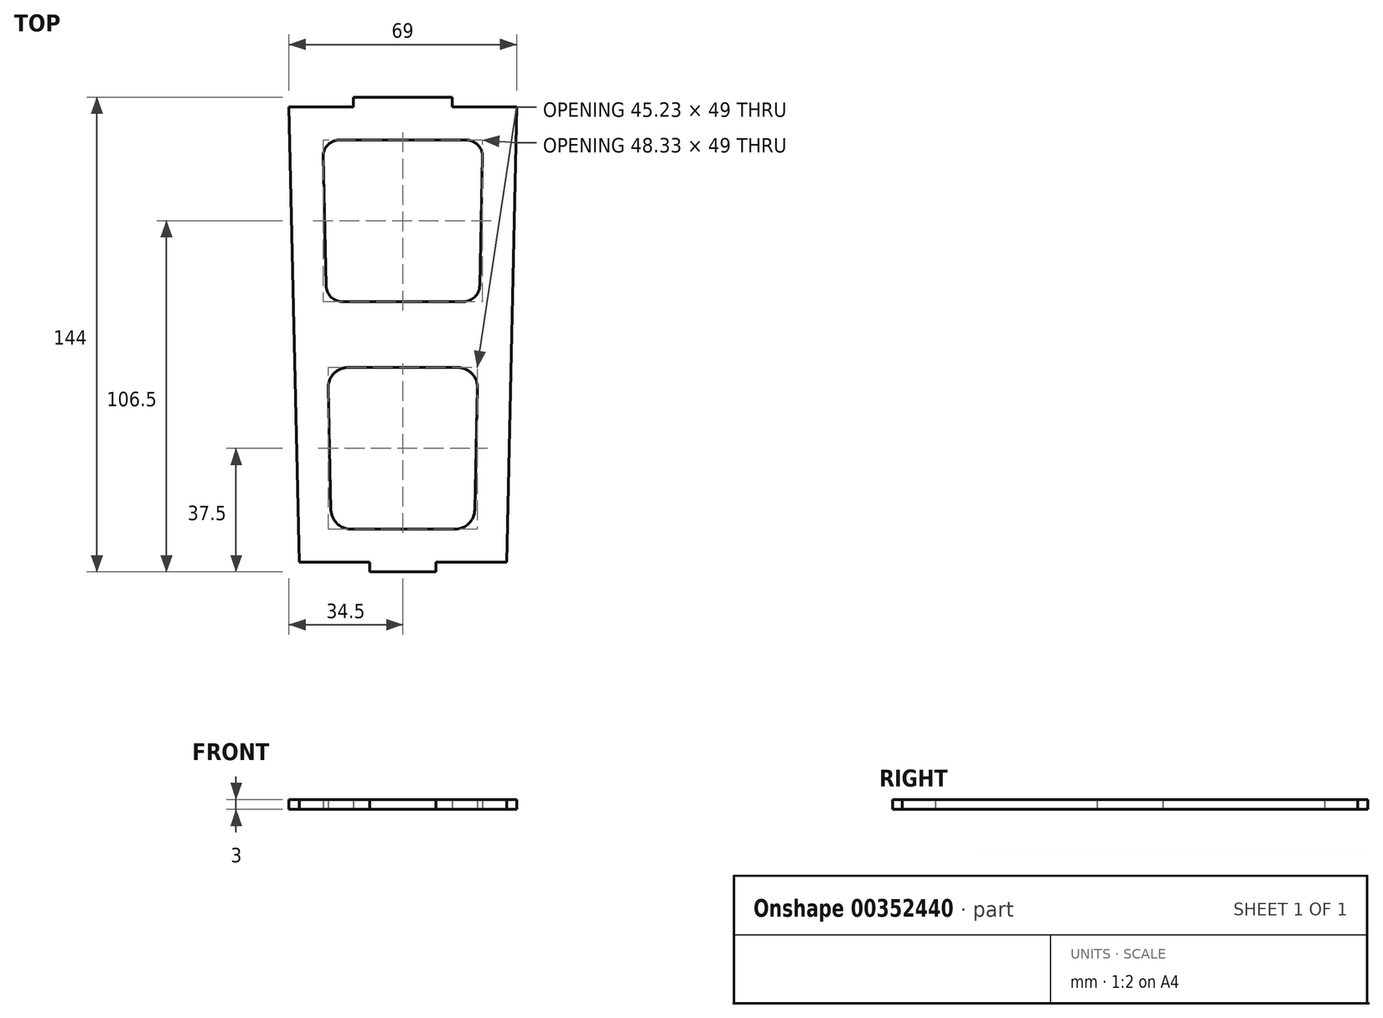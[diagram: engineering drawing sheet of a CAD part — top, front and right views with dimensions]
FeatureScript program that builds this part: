
annotation { "Feature Type Name" : "Feature", "Feature Type Description" : "" }
export const myFeature = defineFeature(function(context is Context, id is Id, definition is map)
    precondition{}
    {
        {
            var Q0;
            Q0=qCreatedBy(makeId("Top.planeOp"),FACE);
            var sketch = newSketch(context, id + "F0", { "sketchPlane" : qUnion([Q0])});
            skLineSegment(sketch, "E0", {"start": v(0, 72) * mm, "end": v(-15, 72) * mm});
            skLineSegment(sketch, "E1", {"start": v(-15, 72) * mm, "end": v(-15, 69) * mm});
            skLineSegment(sketch, "E2", {"start": v(-15, 69) * mm, "end": v(-34.5, 69) * mm});
            skLineSegment(sketch, "E3", {"start": v(-34.5, 69) * mm, "end": v(-31.44, -69) * mm});
            skLineSegment(sketch, "E4", {"start": v(-31.44, -69) * mm, "end": v(-10, -69) * mm});
            skLineSegment(sketch, "E5", {"start": v(-10, -69) * mm, "end": v(-10, -72) * mm});
            skLineSegment(sketch, "E6", {"start": v(-10, -72) * mm, "end": v(0, -72) * mm});
            skLineSegment(sketch, "E7.MirrorCS", {"start": v(0, 72) * mm, "end": v(15, 72) * mm});
            skLineSegment(sketch, "E8.MirrorCS", {"start": v(15, 72) * mm, "end": v(15, 69) * mm});
            skLineSegment(sketch, "E9.MirrorCS", {"start": v(15, 69) * mm, "end": v(34.5, 69) * mm});
            skLineSegment(sketch, "E10.MirrorCS", {"start": v(34.5, 69) * mm, "end": v(31.44, -69) * mm});
            skLineSegment(sketch, "E11.MirrorCS", {"start": v(31.44, -69) * mm, "end": v(10, -69) * mm});
            skLineSegment(sketch, "E12.MirrorCS", {"start": v(10, -69) * mm, "end": v(10, -72) * mm});
            skLineSegment(sketch, "E13.MirrorCS", {"start": v(10, -72) * mm, "end": v(0, -72) * mm});
            skLineSegment(sketch, "E14", {"start": v(-34.5, 69) * mm, "end": v(34.5, 69) * mm, "construction": true});
            skLineSegment(sketch, "E15", {"start": v(-31.44, -69) * mm, "end": v(31.44, -69) * mm, "construction": true});
            skLineSegment(sketch, "E16", {"start": v(-32.97, 0) * mm, "end": v(32.97, 0) * mm, "construction": true});
            skLineSegment(sketch, "E17", {"start": v(-32.97, 0) * mm, "end": v(-34.5, 69) * mm, "construction": true});
            skLineSegment(sketch, "E18", {"start": v(32.97, 0) * mm, "end": v(34.5, 69) * mm, "construction": true});
            skLineSegment(sketch, "E19.0", {"start": v(-18.3, 10) * mm, "end": v(18.3, 10) * mm});
            skLineSegment(sketch, "E19.1", {"start": v(-23.3, 14.89) * mm, "end": v(-24.16, 53.89) * mm});
            skLineSegment(sketch, "E19.2", {"start": v(-19.16, 59) * mm, "end": v(19.16, 59) * mm});
            skLineSegment(sketch, "E19.3", {"start": v(23.3, 14.89) * mm, "end": v(24.16, 53.89) * mm});
            skLineSegment(sketch, "E20", {"start": v(-32.97, 0) * mm, "end": v(-31.44, -69) * mm, "construction": true});
            skLineSegment(sketch, "E21", {"start": v(31.44, -69) * mm, "end": v(32.97, 0) * mm, "construction": true});
            skLineSegment(sketch, "E22.0", {"start": v(-16.61, -10) * mm, "end": v(16.61, -10) * mm});
            skLineSegment(sketch, "E22.1", {"start": v(-22.61, -16.13) * mm, "end": v(-21.8, -53.13) * mm});
            skLineSegment(sketch, "E22.2", {"start": v(-15.8, -59) * mm, "end": v(15.8, -59) * mm});
            skLineSegment(sketch, "E22.3", {"start": v(21.8, -53.13) * mm, "end": v(22.61, -16.13) * mm});
            skPoint(sketch, "E23.visualSharp", {"position": v(-24.28, 59) * mm});
            skArc(sketch, "E23.filletArc", {"start": v(-19.16, 59) * mm, "mid": v(-22.74, 57.5) * mm, "end": v(-24.16, 53.89) * mm});
            skPoint(sketch, "E24.visualSharp", {"position": v(-23.2, 10) * mm});
            skArc(sketch, "E24.filletArc", {"start": v(-23.3, 14.89) * mm, "mid": v(-21.8, 11.43) * mm, "end": v(-18.3, 10) * mm});
            skPoint(sketch, "E25.visualSharp", {"position": v(23.2, 10) * mm});
            skArc(sketch, "E25.filletArc", {"start": v(18.3, 10) * mm, "mid": v(21.8, 11.43) * mm, "end": v(23.3, 14.89) * mm});
            skPoint(sketch, "E26.visualSharp", {"position": v(24.28, 59) * mm});
            skArc(sketch, "E26.filletArc", {"start": v(24.16, 53.89) * mm, "mid": v(22.74, 57.5) * mm, "end": v(19.16, 59) * mm});
            skPoint(sketch, "E27.visualSharp", {"position": v(-22.75, -10) * mm});
            skArc(sketch, "E27.filletArc", {"start": v(-16.61, -10) * mm, "mid": v(-20.9, -11.8) * mm, "end": v(-22.61, -16.13) * mm});
            skPoint(sketch, "E28.visualSharp", {"position": v(22.75, -10) * mm});
            skArc(sketch, "E28.filletArc", {"start": v(22.61, -16.13) * mm, "mid": v(20.9, -11.8) * mm, "end": v(16.61, -10) * mm});
            skPoint(sketch, "E29.visualSharp", {"position": v(21.66, -59) * mm});
            skArc(sketch, "E29.filletArc", {"start": v(15.8, -59) * mm, "mid": v(20, -57.29) * mm, "end": v(21.8, -53.13) * mm});
            skPoint(sketch, "E30.visualSharp", {"position": v(-21.66, -59) * mm});
            skArc(sketch, "E30.filletArc", {"start": v(-21.8, -53.13) * mm, "mid": v(-20, -57.29) * mm, "end": v(-15.8, -59) * mm});
            skSolve(sketch);
        }
        {
            var Q0;
            Q0=makeQuery(id+"F0.imprint","IMPRINT",FACE,{"disambiguationData":[TD([[makeQuery(id+"F0.imprint","IMPRINT",EDGE,{"derivedFrom":sQuery(id+"F0.wireOp",EDGE,"E0")}),1.0]])]});
            extrude(context, id + "F1", {"entities" : qUnion([Q0]), "depth" : 3 * mm, "offsetDistance" : 25 * mm});
        }
    });
